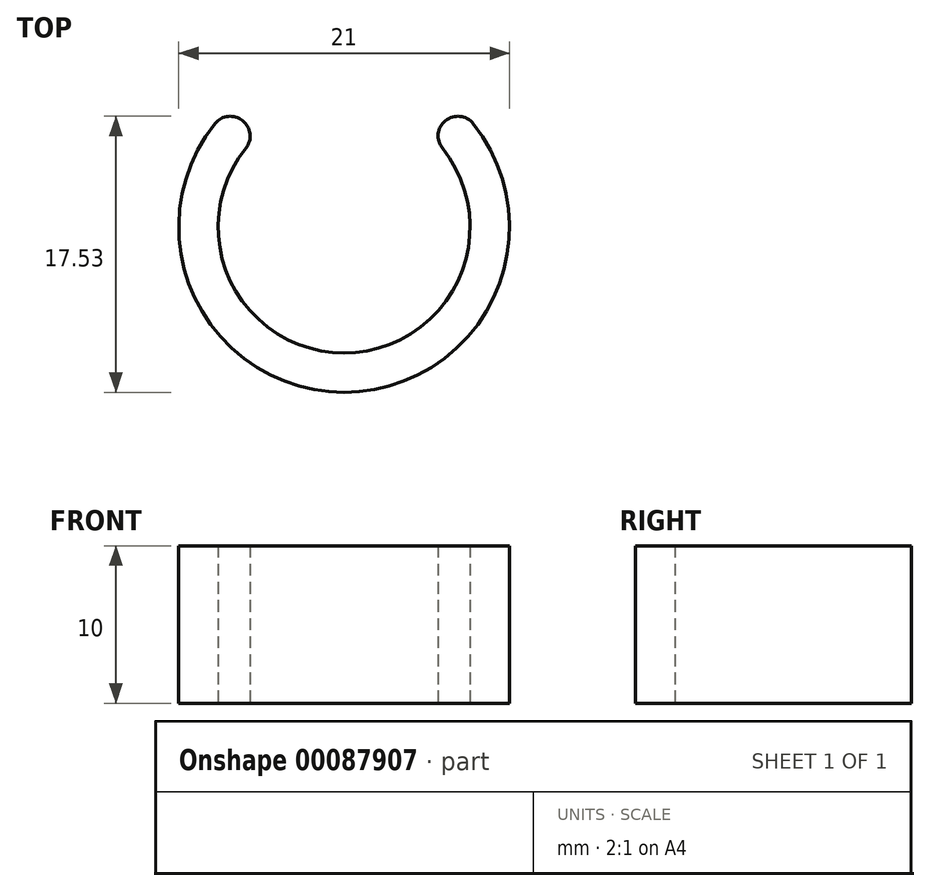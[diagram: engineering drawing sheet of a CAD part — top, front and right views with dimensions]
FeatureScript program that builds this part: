
annotation { "Feature Type Name" : "Feature", "Feature Type Description" : "" }
export const myFeature = defineFeature(function(context is Context, id is Id, definition is map)
    precondition{}
    {
        {
            var Q0;
            Q0=qCreatedBy(makeId("Top.planeOp"),FACE);
            var sketch = newSketch(context, id + "F0", { "sketchPlane" : qUnion([Q0])});
            skCircle(sketch, "E0", {"center": v(0, 0) * mm, "radius": 8 * mm});
            skCircle(sketch, "E1", {"center": v(0, 0) * mm, "radius": 10.5 * mm});
            skPoint(sketch, "E2", {"position": v(-10.5, 0) * mm});
            skPoint(sketch, "E3", {"position": v(10.5, 0) * mm});
            skPoint(sketch, "E4", {"position": v(0, 10.5) * mm});
            skLineSegment(sketch, "E5", {"start": v(0, 0) * mm, "end": v(0, 5) * mm});
            skLineSegment(sketch, "E6", {"start": v(0, 5) * mm, "end": v(6.24, 5) * mm});
            skLineSegment(sketch, "E7", {"start": v(0, 5) * mm, "end": v(-6.24, 5) * mm});
            skLineSegment(sketch, "E8", {"start": v(-6.24, 5) * mm, "end": v(-8.2, 6.56) * mm});
            skLineSegment(sketch, "E9", {"start": v(6.24, 5) * mm, "end": v(8.2, 6.56) * mm});
            skArc(sketch, "E10", {"start": v(-6.24, 5) * mm, "mid": v(-6.44, 6.76) * mm, "end": v(-8.2, 6.56) * mm});
            skArc(sketch, "E11", {"start": v(6.24, 5) * mm, "mid": v(6.44, 6.76) * mm, "end": v(8.2, 6.56) * mm});
            skPoint(sketch, "E12", {"position": v(-8, 0) * mm});
            skPoint(sketch, "E13", {"position": v(8, 0) * mm});
            skPoint(sketch, "E14", {"position": v(0, -10.5) * mm});
            skPoint(sketch, "E15", {"position": v(-13.79, 22.95) * mm});
            skSolve(sketch);
        }
        {
            var Q0;
            {var subQ4=sQuery(id+"F0.wireOp",EDGE,"E8");Q0=makeQuery(id+"F0.imprint","IMPRINT",FACE,{"disambiguationData":[TD([[makeQuery(id+"F0.imprint","IMPRINT",EDGE,{"derivedFrom":subQ4}),1.0]])]});}
            var Q1;
            Q1=makeQuery(id+"F0.imprint","IMPRINT",FACE,{"disambiguationData":[TD([[makeQuery(id+"F0.imprint","IMPRINT",EDGE,{"derivedFrom":sQuery(id+"F0.wireOp",EDGE,"E8")}),-1.0]])]});
            var Q2;
            {var subQ4=sQuery(id+"F0.wireOp",EDGE,"E8");Q2=makeQuery(id+"F0.imprint","IMPRINT",FACE,{"disambiguationData":[TD([[makeQuery(id+"F0.imprint","IMPRINT",EDGE,{"derivedFrom":subQ4}),1.0]])]});}
            var Q3;
            {var subQ4=sQuery(id+"F0.wireOp",EDGE,"E8");Q3=makeQuery(id+"F0.imprint","IMPRINT",FACE,{"disambiguationData":[TD([[makeQuery(id+"F0.imprint","IMPRINT",EDGE,{"derivedFrom":subQ4}),1.0]])]});}
            var Q4;
            Q4=makeQuery(id+"F0.imprint","IMPRINT",FACE,{"disambiguationData":[TD([[makeQuery(id+"F0.imprint","IMPRINT",EDGE,{"derivedFrom":sQuery(id+"F0.wireOp",EDGE,"E9")}),1.0]])]});
            extrude(context, id + "F1", {"entities" : qUnion([Q0, Q1, Q2, Q3, Q4]), "depth" : 10 * mm});
        }
    });
